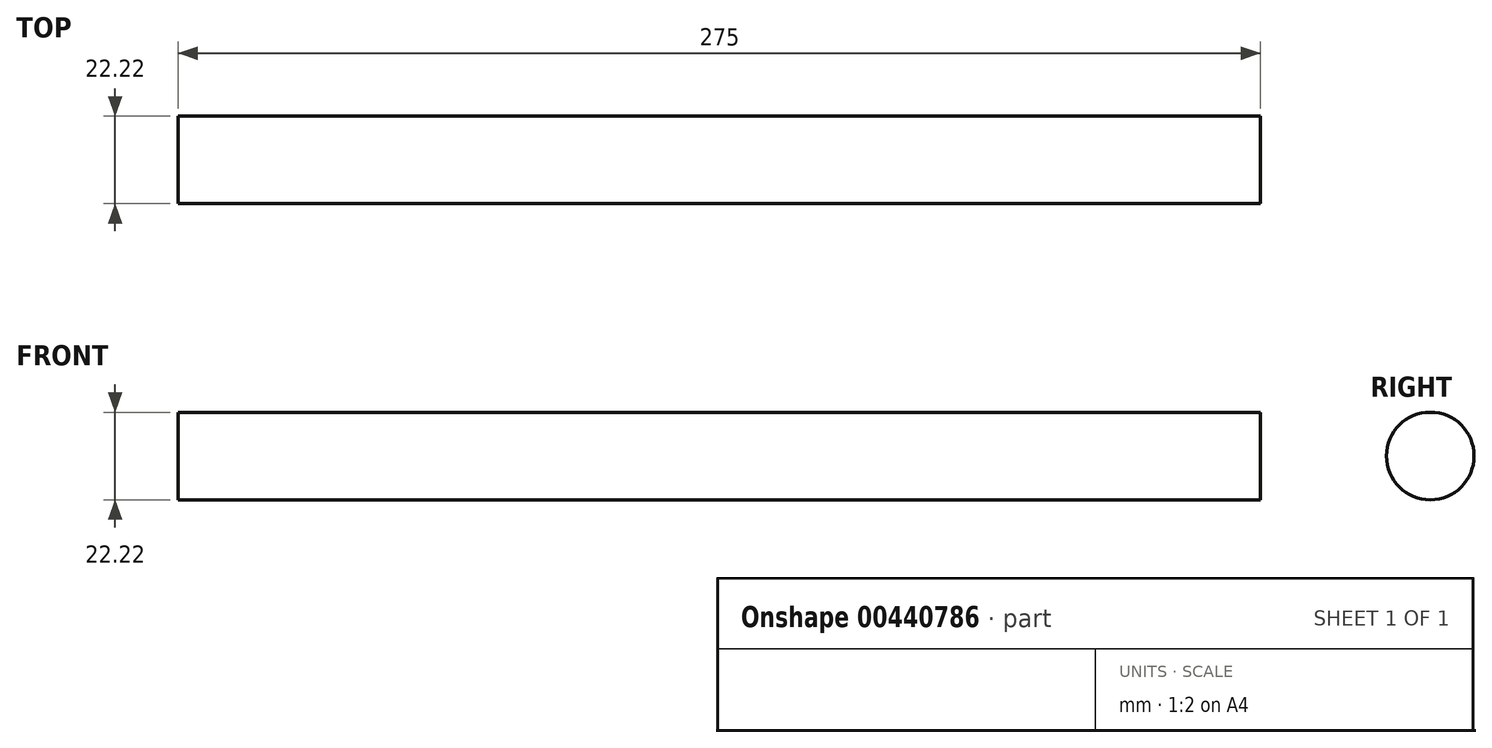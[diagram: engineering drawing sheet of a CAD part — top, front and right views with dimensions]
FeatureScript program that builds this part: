
annotation { "Feature Type Name" : "Feature", "Feature Type Description" : "" }
export const myFeature = defineFeature(function(context is Context, id is Id, definition is map)
    precondition{}
    {
        {
            var Q0;
            Q0=qCreatedBy(makeId("Right.planeOp"),FACE);
            var sketch = newSketch(context, id + "F0", { "sketchPlane" : qUnion([Q0])});
            skCircle(sketch, "E0", {"center": v(0, 0) * mm, "radius": 11.11 * mm});
            skSolve(sketch);
        }
        {
            var Q0;
            Q0=makeQuery(id+"F0.imprint","IMPRINT",FACE,{"disambiguationData":[TD([[makeQuery(id+"F0.imprint","IMPRINT",EDGE,{"derivedFrom":sQuery(id+"F0.wireOp",EDGE,"E0")}),1.0]])]});
            extrude(context, id + "F1", {"entities" : qUnion([Q0]), "depth" : 275 * mm});
        }
    });
